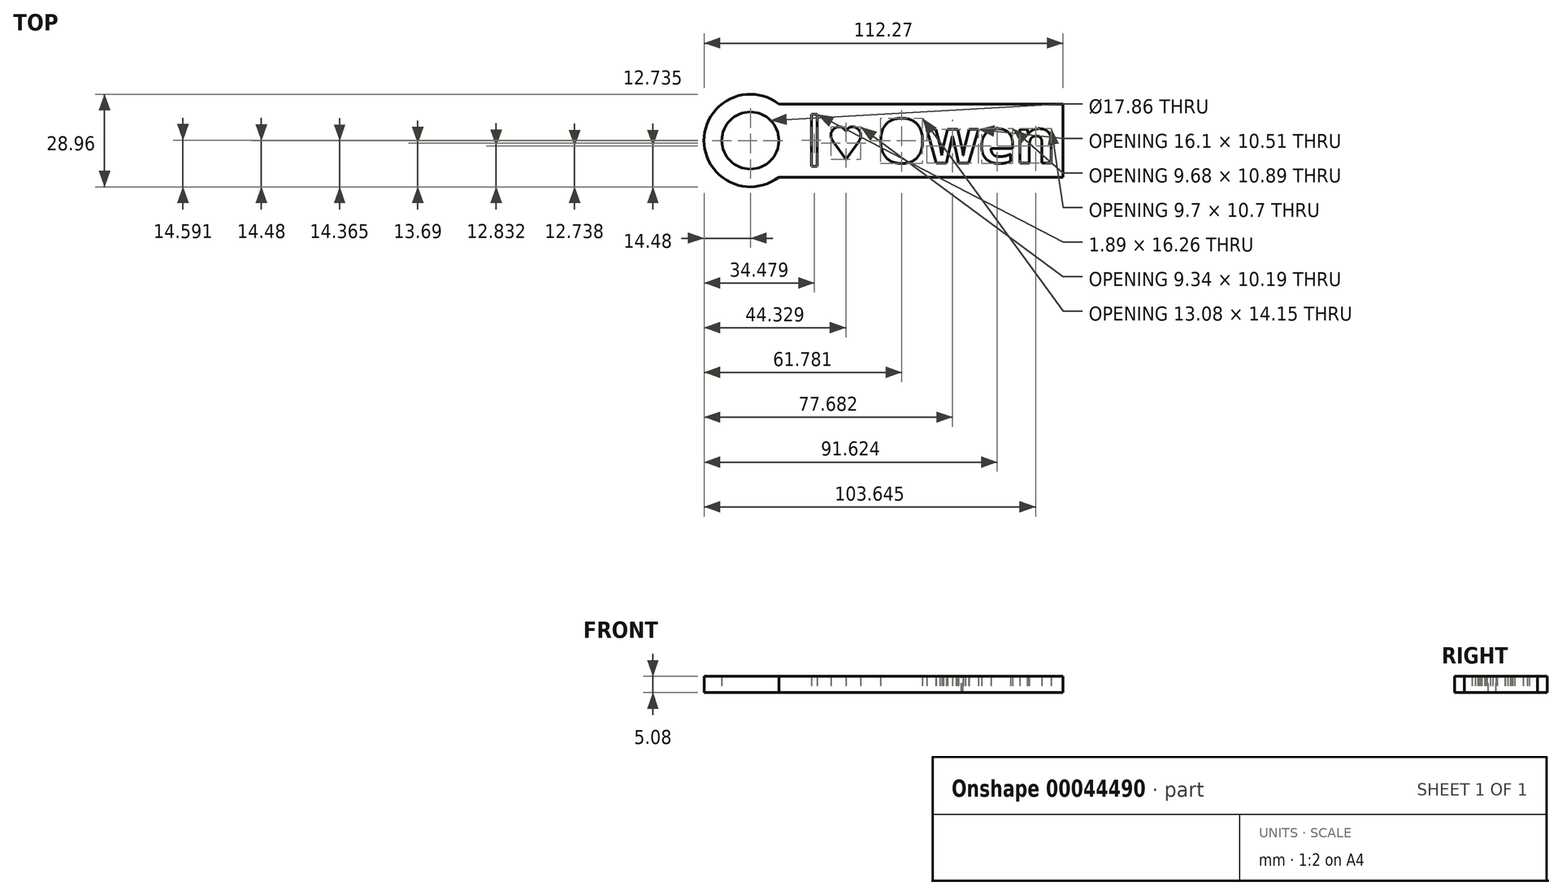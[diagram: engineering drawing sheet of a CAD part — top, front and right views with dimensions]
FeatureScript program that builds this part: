
annotation { "Feature Type Name" : "Feature", "Feature Type Description" : "" }
export const myFeature = defineFeature(function(context is Context, id is Id, definition is map)
    precondition{}
    {
        {
            var Q0;
            Q0=qCreatedBy(makeId("Top.planeOp"),FACE);
            var sketch = newSketch(context, id + "F0", { "sketchPlane" : qUnion([Q0])});
            skLineSegment(sketch, "E0.rect.bottom", {"start": v(44.45, 11.43) * mm, "end": v(-44.45, 11.43) * mm});
            skLineSegment(sketch, "E0.rect.top", {"start": v(44.45, -11.43) * mm, "end": v(-44.45, -11.43) * mm});
            skLineSegment(sketch, "E0.rect.left", {"start": v(44.45, 11.43) * mm, "end": v(44.45, -11.43) * mm});
            skPoint(sketch, "E0.rect.middle", {"position": v(0, 0) * mm});
            skArc(sketch, "E1", {"start": v(-44.45, 11.43) * mm, "mid": v(-67.82, 0) * mm, "end": v(-44.45, -11.43) * mm});
            skCircle(sketch, "E2", {"center": v(-53.34, 0) * mm, "radius": 8.93 * mm});
            skText(sketch, "E3", { "text": "Owen", "fontName": "OpenSans-Bold.ttf"});
            skText(sketch, "E4", { "text": " I ", "fontName": "OpenSans-Regular.ttf"});
            skLineSegment(sketch, "E5", {"start": v(-23.5, -5.88) * mm, "end": v(-19.3, 0) * mm});
            skArc(sketch, "E6", {"start": v(-19.3, 0) * mm, "mid": v(-19.02, 2.64) * mm, "end": v(-21.1, 4.28) * mm});
            skArc(sketch, "E7", {"start": v(-21.1, 4.28) * mm, "mid": v(-22.54, 4.01) * mm, "end": v(-23.5, 2.9) * mm});
            skArc(sketch, "E8.MirrorCS", {"start": v(-25.88, 4.28) * mm, "mid": v(-24.45, 4.01) * mm, "end": v(-23.5, 2.9) * mm});
            skArc(sketch, "E9.MirrorCS", {"start": v(-27.67, 0) * mm, "mid": v(-27.97, 2.64) * mm, "end": v(-25.88, 4.28) * mm});
            skLineSegment(sketch, "E10.MirrorCS", {"start": v(-23.5, -5.88) * mm, "end": v(-27.67, 0) * mm});
            const initialGuessF0  = {"E3": [-0.0137, -0.007, 1, 0, 0.01386], "E4": [-0.04244, -0.00802, 1, 0, 0.0164]};
            skSetInitialGuess(sketch, initialGuessF0);
            skSolve(sketch);
        }
        {
            var Q0;
            Q0=makeQuery(id+"F0.imprint","IMPRINT",FACE,{"disambiguationData":[TD([[makeQuery(id+"F0.imprint","IMPRINT",EDGE,{"derivedFrom":sQuery(id+"F0.wireOp",EDGE,"E0.rect.bottom")}),1.0]])]});
            extrude(context, id + "F1", {"entities" : qUnion([Q0]), "depth" : 5.08 * mm});
        }
    });
